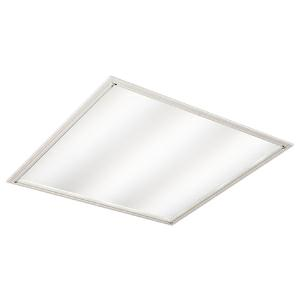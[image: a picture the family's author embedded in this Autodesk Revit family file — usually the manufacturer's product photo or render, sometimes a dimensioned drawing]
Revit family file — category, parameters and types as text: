
# Revit family: 3f_filippi_-_l_320_lgs_3f_filippi_-_21586_-_l_323x10w_led_dali_lgs_596x596
name_source: partatom
category: Lighting Fixtures
units: mm (PartAtom-declared; Revit-internal decimal feet)

## family parameters
Cut with Voids When Loaded = No
Host = Face
Light Source = No
Part Type = Normal
Room Calculation Point = No
Round Connector Dimension = Use Diameter
Shared = No

## types (1)
- 3F Filippi - L 320 LGS (1 x LED, 3178 lm, 34 W, 4000 K)
    Apparent Load = 34 VA
    Approval mark = ENEC
    CIE Flux Codes = 64 89 98 100 100
    Color Rendering = 80
    Color Temperature = 4000 K
    Control Gear = Electronic transformer
    Default Elevation = 1800 mm
    Description = ILLUMINOTECHNICAL
Luminous efficiency 100% (DLOR 100%, ULOR 0%).
Initial luminous flux of the luminaire 3178 lm.
Direct symmetric distribution.
Installation Interdistance Transv.D = 1.17 x hu - Long.D = 1.16 x hu.
Average luminance <1500 cd/m² for radial angles >65°.
Tabular UGR (CIE 117 - 4H-8H; S=0.25H; 70/50/20): RUG 17.2 - 17.2.
Beam angle: 85° - 84°.
Luminous efficacy 93 lm/W.
Lifetime (L93/B10): 30000 h. (tq+25°C)
Lifetime (L90/B10): 50000 h. (tq+25°C)
Lifetime (L85/B10): 80000 h. (tq+25°C)
Lifetime (L80/B10): 100000 h. (tq+25°C)
Sudden decreased luminous flux after 50000 hours: 0% (C0).
Photobiological safety in compliance with IEC/TR 62778: RG0 risk exempt, (IEC 62471).
In compliance with IEC/EN 62722-2-1 - IEC/EN 62717 standards.

SOURCE
3 linear LED modules 10W/840.
Energy efficiency class (UE 2019/2020 - UE 2019/2015): D.
CIE 13.3 Colour rendering index: CRI >80 (R9 <50%).
IES TM-30 Fidelity Index: Rf = 84 Rg = 95.
CCT nominal colour temperature 4000 K.
Colour initial tolerance (MacAdam): SDCM 2.

MECHANICAL
Housing in hot-galvanised steel, painted in white polyester.
Micro-prismatic flat diffuser in transparent methacrylate (PMMA), multilenticular exterior, anti-glare, locked to the white painted aluminium perimetral frame, sealing gasket, hinged opening.
Anti-glare opal polycarbonate filter for brightness uniformity.
Luminaire with limited surface temperature. - D - (EN 60598-2-24)
Dimensions: 596x596 mm, height 80 mm. Weight 4.5 kg.
IP54 protection degree for exposed part, IP20 for recessed part.
Mechanical strength to impacts IK06 (1 joule).
Glow-wire test resistance 650°C.

ELECTRICAL
Halogen Free DALI-2 DATI (Parts 251, 252, 253), PUSH-DIM, electronic wiring 230V-50/60Hz, power factor 0.95 at full load, THD <25%, constant output current, SELV, class I, 1 driver, 1 DALI addresse.
Power of the luminaire 34 W.
CE - IEC 60598-1 - EN 60598-1.
SAFE FLICKER: PstLM=<1 and SVM=<0.4 (IEC TR 61547-1 and IEC TR 63158), to ensure a more comfortable and safe light.
Luminaire compliant with EN 60598-2-22 for power supply from a centralised emergency system CPSS (Central Power Supply System), not incorporated in the luminaire - high risk areas excluded. The default power and flux are 100% in AC and 15% in DC.
Ambient temperature from 0°C to +25°C.
Temperature class T6 max 85°C.
Relative humidity UR: <85%.

INSTALLATION
Lay-in recessed fitting.
On request: pull-up recessed fitting with brackets.
False ceiling carving: 580x580 mm.
All accessories dedicated to this product are available on the Catalog and on our website www.3F-Filippi.com.

APPLICATIONS
Environments: sterilized, aseptic.
In environments with VDU's, managerial offices and staterooms, environments involving accurate visual tasks where a diffused and soft light for an optimum visual comfort and the source total shielding are required.

LIGHT MANAGEMENT
Recommended minimum setting: 10%.
The luminaire, equipped with (DALI-2 DATI) driver, can be controlled manually with 3F Easy Dim technology or automatically/manually with wired or wireless DALI/D2D control systems.
The D2D driver guarantees interoperability with other devices with the same certification by making the following information available:
Device Data (Part 251), Energy Report (Part 252), Diagnosis & Maintenance (Part 253).
In electrical systems without a regulation system (manual or automatic) and DALI bus, a suitable jumper must be made on the DA-DA terminals of the appliance.

WARNING
Luminaire designed for disposal/recycling at end-of-life.
Replaceable (LED only) light source by a professional. Replaceable control gear by a professional.
    Height = 0 mm  [stored 0 ft]
    Lamp = 1 x LED
    Lamp Light Flux = 3178 lm
    Lamp Power = 34 W
    Lamp count = 1
    Length = 596 mm
    Lifetime = 50000 h
    Luminous efficacy = 93 lm/W
    Manufacturer = 3F Filippi
    ModVariant = No
    Model = 3F Filippi - 21586 - L 323x10W LED DALI LGS 596x596
    Mounting Place = Ceiling
    Mounting Type = Recessed
    Number of Poles = 1
    OnlyDefault = Yes
    Power Factor = 1
    Product Name = 3F Filippi - L 320 LGS
    Product group = recessed luminaire
    ProductGroupID = 4
    Protection Class = Protection class I
    Protection Degree = IP 20
    RLX_Detail_Level = 1
    RLX_Emergency_Light_Flux = 0 lm
    RLX_Emergency_Type = 0
    RLX_Emergency_Type_DB = No
    RlxData = <blob elided: 36345 chars, md5=ac011625>
    Socket = socket
    Standby Power = 0 W
    System Light Flux = 3178 lm
    System Power = 34 W
    Type Comments = Product without accessories
    Type Image = 3ffilippi_l_320_led_lgs.jpg
    URL = http://relux.com
    VarID = ---
    Voltage = 0 V
    Weight = 0.00 kg
    Width = 596 mm

note: [stored X ft] marks values corroborated as IEEE doubles in the binary element streams (Revit-internal decimal feet)

## geometry (parser evidence)
native form markers: Blend x4, Sweep x9
no freeform markers — native parametric forms only
